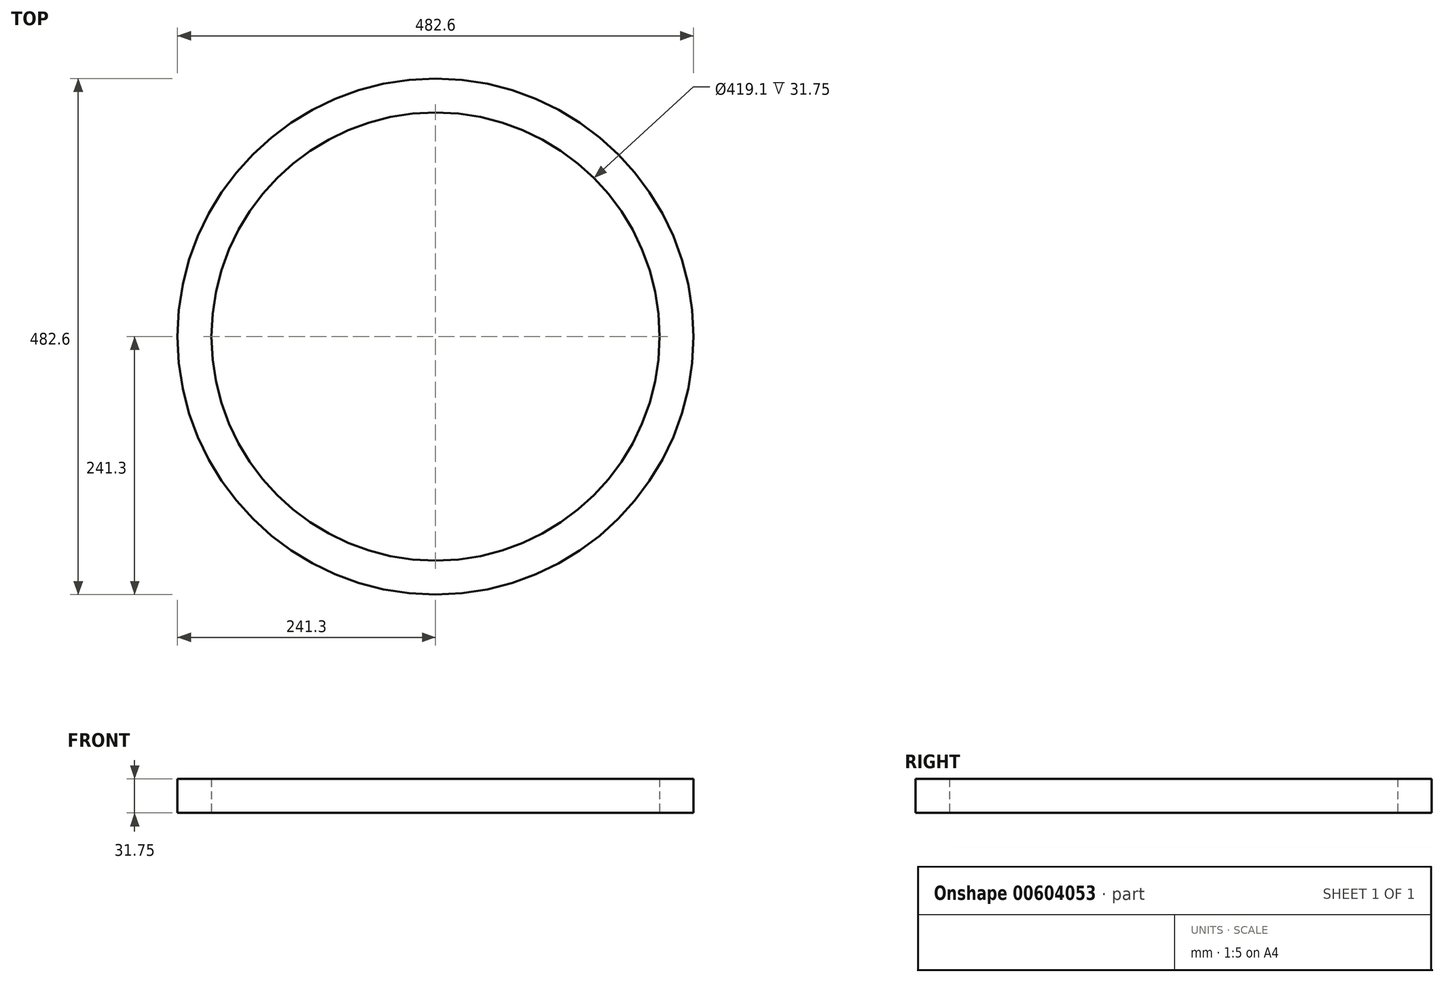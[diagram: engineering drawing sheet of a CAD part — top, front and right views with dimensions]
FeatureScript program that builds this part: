
annotation { "Feature Type Name" : "Feature", "Feature Type Description" : "" }
export const myFeature = defineFeature(function(context is Context, id is Id, definition is map)
    precondition{}
    {
        {
            var Q0;
            Q0=qCreatedBy(makeId("Top.planeOp"),FACE);
            var sketch = newSketch(context, id + "F0", { "sketchPlane" : qUnion([Q0])});
            skCircle(sketch, "E0", {"center": v(0, 0) * mm, "radius": 241.3 * mm});
            skCircle(sketch, "E1.0", {"center": v(0, 0) * mm, "radius": 209.55 * mm});
            skSolve(sketch);
        }
        {
            var Q0;
            Q0 = qSketchRegion(id + "F0", true);
            extrude(context, id + "F1", {"entities" : qUnion([Q0]), "depth" : 31.75 * mm, "offsetDistance" : 25.4 * mm});
        }
    });
